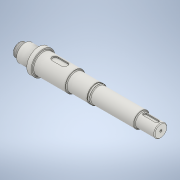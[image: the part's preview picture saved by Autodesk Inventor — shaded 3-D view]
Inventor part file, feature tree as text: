
AUTODESK INVENTOR PART (.ipt)
format: ipt  version: 2020 (Build 240168000, 168)  size: 247,808 bytes
history: native  units: mm
features: other x6, sketch x5, extrude x4, chamfer x2, revolve x1, plane x1, thread x1, fillet x1, hole x1
ambient origin geometry x6: Origin, XZ Plane, XY Plane, X Axis, Y Axis, Z Axis
bodies: 实体1 (feature_tree)
feature tree (22):
  revolve  "旋转1"  [1 undecoded]
  other  "键槽2"
  other  "键槽1"
  plane  "工作平面1"
  extrude  "拉伸2"  Depth=46.0mm
  extrude  "拉伸3"  Depth=36.0mm
  extrude  "拉伸4"  TaperAngle=0.0deg  [1 undecoded]
  extrude  "拉伸5"  Depth=1.6mm
  thread  "螺纹1"  [1 undecoded]
  chamfer  "倒角1"  Distance=37.5mm
  chamfer  "倒角2"  Distance=2.0mm
  fillet  "圆角1"  Radius=15.0mm
  hole  "孔1"  [1 undecoded]
  other  "起始平面"
  other  "主草图"
  other  "iFeature3:1"
  other  "iFeature3:2"
  sketch  "草图4"  dims[d0=0.0mm d1=0.0mm d2=0.0mm d3=40.0mm]
  sketch  "草图5"  dims[d4=55.0mm d5=46.0mm]
  sketch  "草图6"  dims[d6=40.0mm d7=36.0mm]
  sketch  "草图7"  dims[d8=30.0mm d9=0.0mm]
  sketch  "草图8"  dims[d12=40.0mm d13=40.0mm d14=-5.5mm d15=37.5mm d16=2.0mm d17=0.0mm d18=15.0mm d19=0.0mm d20=30.0mm d21=14.0mm d22=0.0mm d23=28.4mm d24=30.0mm d25=3.0mm d26=0.0mm d27=11.0mm d28=0.0mm d29=1.6mm d30=2.0mm d31=45.0deg d32=1.6mm d33=2.0mm d34=45.0deg d35=1.6mm d36=20.0mm d37=4.917mm d38=12.0mm d39=4.0mm d40=2.0mm d41=90.0deg d42=16.0mm d43=20.594885mm]
note: 4 required parameter values undecoded (feature->parameter linkage not recoverable at this tier; creation-order binding heuristic only, values carry confidence <= 0.55)